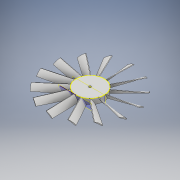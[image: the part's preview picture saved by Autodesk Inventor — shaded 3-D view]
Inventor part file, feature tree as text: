
AUTODESK INVENTOR PART (.ipt)
format: ipt  version: 2018 (Build 220112000, 112)  size: 356,352 bytes
history: native  units: mm
features: sketch x6, extrude x3, plane x2, sweep x1, pattern_circular x1
ambient origin geometry x8: Origin, YZ Plane, XZ Plane, XY Plane, X Axis, Y Axis, Z Axis, Center Point
bodies: Solid1 (feature_tree)
feature tree (13):
  extrude  "Extrusion1"  Depth=25.0mm
  sketch  "Sketch2"  dims[d3=2.0mm d4=2.0mm]
  plane  "Work Plane1"
  sweep  "Sweep1"
  extrude  "Extrusion2"  Depth=25.0mm
  pattern_circular  "Circular Pattern1"  Count=14 Angle=360.0deg
  plane  "Work Plane3"
  extrude  "Extrusion3"  Depth=3.0mm TaperAngle=0.0deg
  sketch  "Sketch1"  dims[d0=2.1mm d1=25.0mm]
  sketch  "Sketch3"  dims[d5=5.0mm d6=0.0mm d13=25.0mm]
  sketch  "Sketch5"  dims[d14=0.0mm d15=4.363323mm]
  sketch  "Sketch6"  dims[d16=1.0mm d17=0.0mm d18=140.0mm d19=360.0deg]
  sketch  "Sketch9"  dims[d21=12.5mm d22=3.0mm d23=0.0mm]
